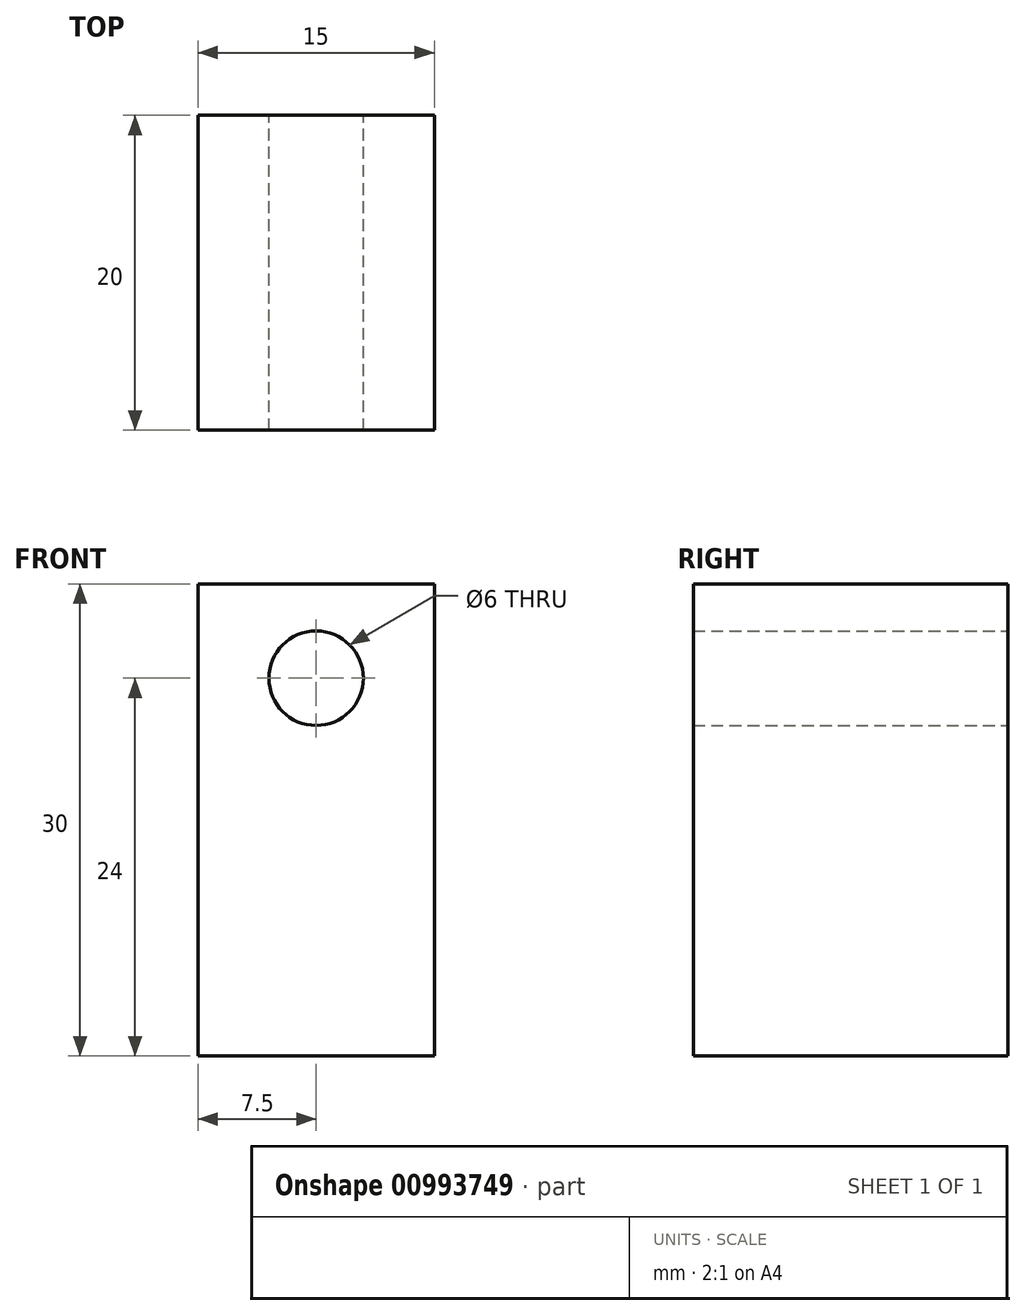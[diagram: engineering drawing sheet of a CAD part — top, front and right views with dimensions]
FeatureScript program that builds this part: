
annotation { "Feature Type Name" : "Feature", "Feature Type Description" : "" }
export const myFeature = defineFeature(function(context is Context, id is Id, definition is map)
    precondition{}
    {
        {
            var Q0;
            Q0=qCreatedBy(makeId("Front.planeOp"),FACE);
            var sketch = newSketch(context, id + "F0", { "sketchPlane" : qUnion([Q0])});
            skLineSegment(sketch, "E0.bottom", {"start": v(0, 0) * mm, "end": v(15, 0) * mm});
            skLineSegment(sketch, "E0.top", {"start": v(0, 30) * mm, "end": v(15, 30) * mm});
            skLineSegment(sketch, "E0.left", {"start": v(0, 0) * mm, "end": v(0, 30) * mm});
            skLineSegment(sketch, "E0.right", {"start": v(15, 0) * mm, "end": v(15, 30) * mm});
            skCircle(sketch, "E1", {"center": v(7.5, 24) * mm, "radius": 3 * mm});
            skPoint(sketch, "E2", {"position": v(7.5, 30) * mm});
            skLineSegment(sketch, "E3", {"start": v(7.5, 30) * mm, "end": v(7.5, 0) * mm, "construction": true});
            skSolve(sketch);
        }
        {
            var Q0;
            Q0=makeQuery(id+"F0.imprint","IMPRINT",FACE,{"disambiguationData":[TD([[makeQuery(id+"F0.imprint","IMPRINT",EDGE,{"derivedFrom":sQuery(id+"F0.wireOp",EDGE,"E0.bottom")}),1.0]])]});
            extrude(context, id + "F1", {"entities" : qUnion([Q0]), "depth" : 20 * mm, "offsetDistance" : 25 * mm});
        }
    });
